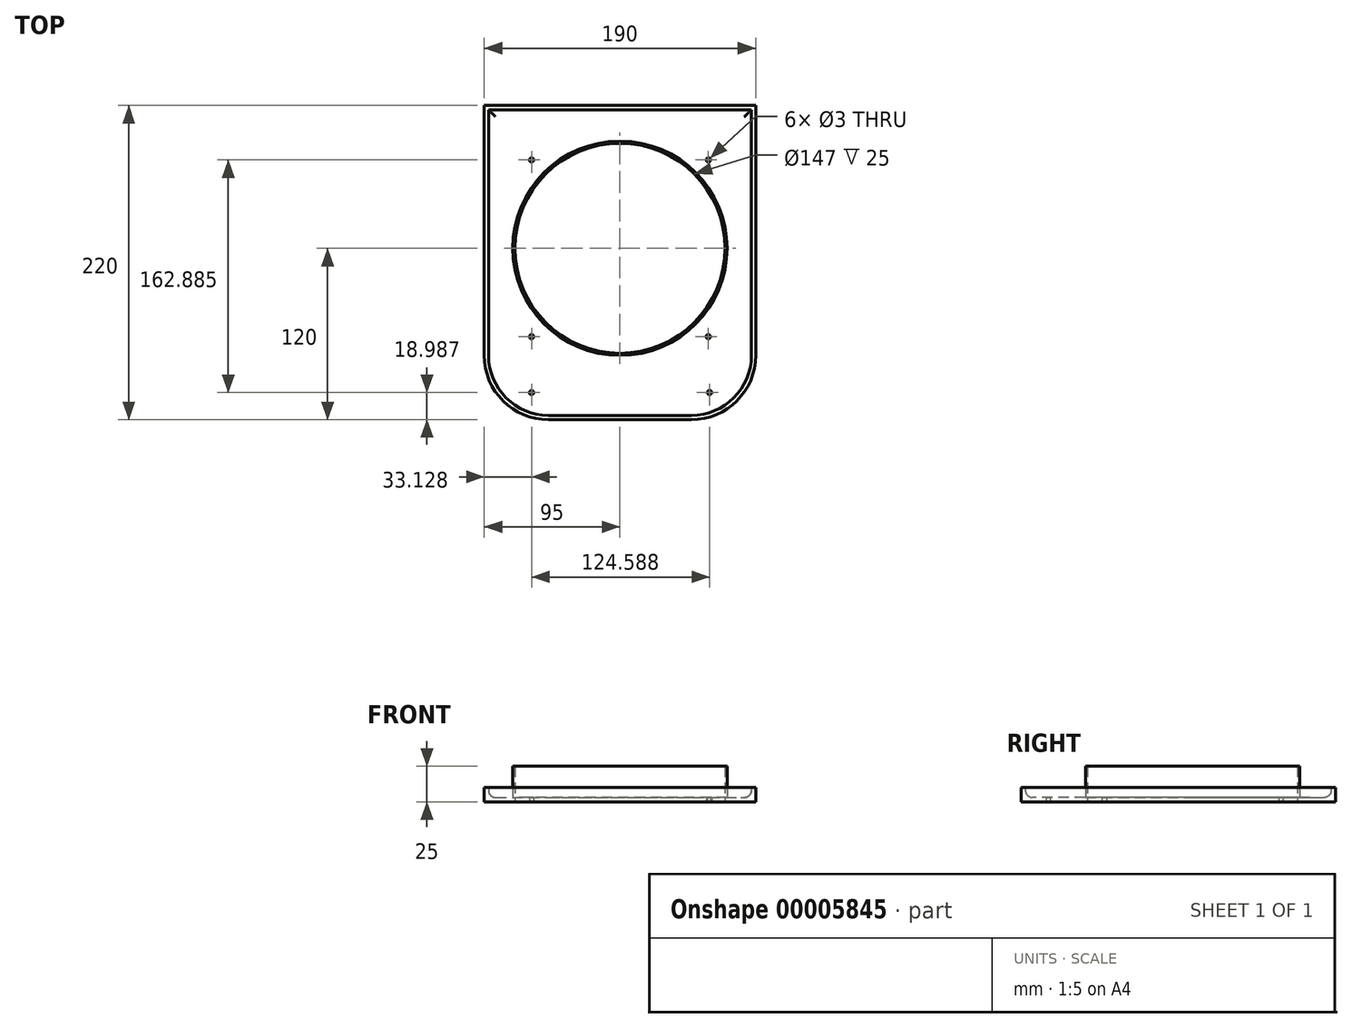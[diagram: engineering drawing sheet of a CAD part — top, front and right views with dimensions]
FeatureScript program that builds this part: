
annotation { "Feature Type Name" : "Feature", "Feature Type Description" : "" }
export const myFeature = defineFeature(function(context is Context, id is Id, definition is map)
    precondition{}
    {
        {
            var Q0;
            Q0=qCreatedBy(makeId("Top.planeOp"),FACE);
            var sketch = newSketch(context, id + "F0", { "sketchPlane" : qUnion([Q0])});
            skCircle(sketch, "E0", {"center": v(0, 0) * mm, "radius": 75 * mm});
            skCircle(sketch, "E1", {"center": v(0, 0) * mm, "radius": 73.5 * mm});
            skLineSegment(sketch, "E2", {"start": v(0, 0) * mm, "end": v(0, 133.7) * mm, "construction": true});
            skLineSegment(sketch, "E3", {"start": v(0, 100) * mm, "end": v(100, 100) * mm, "construction": true});
            skLineSegment(sketch, "E4", {"start": v(100, 100) * mm, "end": v(100, -75) * mm, "construction": true});
            skLineSegment(sketch, "E5", {"start": v(50, -125) * mm, "end": v(0, -125) * mm, "construction": true});
            skPoint(sketch, "E6.visualSharp", {"position": v(100, -125) * mm});
            skArc(sketch, "E6.filletArc", {"start": v(50, -125) * mm, "mid": v(85.36, -110.36) * mm, "end": v(100, -75) * mm, "construction": true});
            skLineSegment(sketch, "E7.0.MirrorCS", {"start": v(0, 100) * mm, "end": v(-100, 100) * mm, "construction": true});
            skLineSegment(sketch, "E7.1.MirrorCS", {"start": v(-50, -125) * mm, "end": v(0, -125) * mm, "construction": true});
            skLineSegment(sketch, "E7.2.MirrorCS", {"start": v(-100, 100) * mm, "end": v(-100, -75) * mm, "construction": true});
            skArc(sketch, "E7.3.MirrorCS", {"start": v(-50, -125) * mm, "mid": v(-85.36, -110.36) * mm, "end": v(-100, -75) * mm, "construction": true});
            skLineSegment(sketch, "E8", {"start": v(95, 100) * mm, "end": v(-95, 100) * mm});
            skLineSegment(sketch, "E9.0", {"start": v(57.6, 97) * mm, "end": v(-92, 97) * mm});
            skLineSegment(sketch, "E10", {"start": v(-95, 97) * mm, "end": v(-95, 82) * mm});
            skLineSegment(sketch, "E11", {"start": v(-57.6, 82) * mm, "end": v(95, 82) * mm, "construction": true});
            skLineSegment(sketch, "E12.left", {"start": v(-95, 82) * mm, "end": v(-95, 97) * mm});
            skLineSegment(sketch, "E13.1.0.0", {"start": v(-57.6, 97) * mm, "end": v(-57.6, 82) * mm});
            skLineSegment(sketch, "E13.1.0.1", {"start": v(-54.6, 82) * mm, "end": v(-54.6, 97) * mm});
            skLineSegment(sketch, "E13.1.0.2", {"start": v(-57.6, 97) * mm, "end": v(-54.6, 97) * mm});
            skLineSegment(sketch, "E13.1.0.3", {"start": v(-57.6, 82) * mm, "end": v(-54.6, 82) * mm});
            skLineSegment(sketch, "E13.2.0.0", {"start": v(-20.2, 97) * mm, "end": v(-20.2, 82) * mm});
            skLineSegment(sketch, "E13.2.0.1", {"start": v(-17.2, 82) * mm, "end": v(-17.2, 97) * mm});
            skLineSegment(sketch, "E13.2.0.3", {"start": v(-20.2, 82) * mm, "end": v(-17.2, 82) * mm});
            skLineSegment(sketch, "E13.3.0.0", {"start": v(17.2, 97) * mm, "end": v(17.2, 82) * mm});
            skLineSegment(sketch, "E13.3.0.1", {"start": v(20.2, 82) * mm, "end": v(20.2, 97) * mm});
            skLineSegment(sketch, "E13.3.0.3", {"start": v(17.2, 82) * mm, "end": v(20.2, 82) * mm});
            skLineSegment(sketch, "E13.4.0.0", {"start": v(54.6, 97) * mm, "end": v(54.6, 82) * mm});
            skLineSegment(sketch, "E13.4.0.1", {"start": v(57.6, 82) * mm, "end": v(57.6, 97) * mm});
            skLineSegment(sketch, "E13.4.0.3", {"start": v(54.6, 82) * mm, "end": v(57.6, 82) * mm});
            skLineSegment(sketch, "E13.direction1", {"start": v(-92, 82) * mm, "end": v(-57.6, 82) * mm, "construction": true});
            skLineSegment(sketch, "E14.0.5.0", {"start": v(92, 97) * mm, "end": v(92, 82) * mm});
            skLineSegment(sketch, "E14.9.5.0", {"start": v(92, 82) * mm, "end": v(95, 82) * mm});
            skLineSegment(sketch, "E15", {"start": v(0, 0) * mm, "end": v(128.67, 128.67) * mm, "construction": true});
            skCircle(sketch, "E16", {"center": v(61.87, 61.87) * mm, "radius": 1.5 * mm});
            skCircle(sketch, "E17.1.0", {"center": v(-61.87, 61.87) * mm, "radius": 1.5 * mm});
            skCircle(sketch, "E17.2.0", {"center": v(-61.87, -61.87) * mm, "radius": 1.5 * mm});
            skCircle(sketch, "E17.3.0", {"center": v(61.87, -61.87) * mm, "radius": 1.5 * mm});
            skCircle(sketch, "E18", {"center": v(0, 0) * mm, "radius": 87.5 * mm, "construction": true});
            skArc(sketch, "E19.1", {"start": v(50, -120) * mm, "mid": v(81.82, -106.82) * mm, "end": v(95, -75) * mm});
            skLineSegment(sketch, "E19.2", {"start": v(50, -120) * mm, "end": v(0, -120) * mm});
            skLineSegment(sketch, "E19.3", {"start": v(-50, -120) * mm, "end": v(0, -120) * mm});
            skArc(sketch, "E19.4", {"start": v(-50, -120) * mm, "mid": v(-81.82, -106.82) * mm, "end": v(-95, -75) * mm});
            skCircle(sketch, "E20", {"center": v(-61.87, -101.01) * mm, "radius": 1.5 * mm});
            skCircle(sketch, "E21", {"center": v(62.72, -101.01) * mm, "radius": 1.5 * mm});
            skLineSegment(sketch, "E22", {"start": v(-95, 100) * mm, "end": v(-95, -75) * mm});
            skArc(sketch, "E23.1", {"start": v(50, -117) * mm, "mid": v(79.7, -104.7) * mm, "end": v(92, -75) * mm});
            skLineSegment(sketch, "E23.2", {"start": v(50, -117) * mm, "end": v(0, -117) * mm});
            skLineSegment(sketch, "E23.3", {"start": v(-50, -117) * mm, "end": v(0, -117) * mm});
            skArc(sketch, "E23.4", {"start": v(-50, -117) * mm, "mid": v(-79.7, -104.7) * mm, "end": v(-92, -75) * mm});
            skLineSegment(sketch, "E23.5", {"start": v(-92, 97) * mm, "end": v(-92, -75) * mm});
            skLineSegment(sketch, "E24", {"start": v(95, 82) * mm, "end": v(95, 100) * mm});
            skLineSegment(sketch, "E25", {"start": v(57.6, 97) * mm, "end": v(92, 97) * mm});
            skLineSegment(sketch, "E26", {"start": v(92, -75) * mm, "end": v(92, 82) * mm});
            skLineSegment(sketch, "E27", {"start": v(95, -75) * mm, "end": v(95, 82) * mm});
            skLineSegment(sketch, "E28", {"start": v(-95, 82) * mm, "end": v(-92, 82) * mm});
            skSolve(sketch);
        }
        {
            var Q0;
            Q0=makeQuery(id+"F0.imprint","IMPRINT",FACE,{"disambiguationData":[TD([[makeQuery(id+"F0.imprint","IMPRINT",EDGE,{"derivedFrom":sQuery(id+"F0.wireOp",EDGE,"E0")}),-1.0]])]});
            var Q1;
            {var subQ1=sQuery(id+"F0.wireOp",EDGE,"E13.4.0.0");Q1=makeQuery(id+"F0.imprint","IMPRINT",FACE,{"disambiguationData":[TD([[makeQuery(id+"F0.imprint","IMPRINT",EDGE,{"derivedFrom":subQ1}),1.0]])]});}
            var Q2;
            {var subQ1=sQuery(id+"F0.wireOp",EDGE,"E13.3.0.0");Q2=makeQuery(id+"F0.imprint","IMPRINT",FACE,{"disambiguationData":[TD([[makeQuery(id+"F0.imprint","IMPRINT",EDGE,{"derivedFrom":subQ1}),1.0]])]});}
            var Q3;
            {var subQ1=sQuery(id+"F0.wireOp",EDGE,"E13.2.0.0");Q3=makeQuery(id+"F0.imprint","IMPRINT",FACE,{"disambiguationData":[TD([[makeQuery(id+"F0.imprint","IMPRINT",EDGE,{"derivedFrom":subQ1}),1.0]])]});}
            var Q4;
            Q4=makeQuery(id+"F0.imprint","IMPRINT",FACE,{"disambiguationData":[TD([[makeQuery(id+"F0.imprint","IMPRINT",EDGE,{"derivedFrom":sQuery(id+"F0.wireOp",EDGE,"E13.1.0.0")}),1.0]])]});
            var Q5;
            Q5=makeQuery(id+"F0.imprint","IMPRINT",FACE,{"disambiguationData":[TD([[makeQuery(id+"F0.imprint","IMPRINT",EDGE,{"derivedFrom":sQuery(id+"F0.wireOp",EDGE,"E19.1")}),1.0]])]});
            var Q6;
            {var subQ3=sQuery(id+"F0.wireOp",EDGE,"E8");Q6=makeQuery(id+"F0.imprint","IMPRINT",FACE,{"disambiguationData":[TD([[makeQuery(id+"F0.imprint","IMPRINT",EDGE,{"derivedFrom":subQ3}),1.0]])]});}
            extrude(context, id + "F1", {"entities" : qUnion([Q0, Q1, Q2, Q3, Q4, Q5, Q6]), "depth" : 3 * mm});
        }
        {
            var Q0;
            Q0=makeQuery(id+"F0.imprint","IMPRINT",FACE,{"disambiguationData":[TD([[makeQuery(id+"F0.imprint","IMPRINT",EDGE,{"derivedFrom":sQuery(id+"F0.wireOp",EDGE,"E0")}),1.0]])]});
            extrude(context, id + "F2", {"entities" : qUnion([Q0]), "operationType" : NewBodyOperationType.ADD, "depth" : 25 * mm});
        }
        {
            var Q0;
            Q0=makeQuery(id+"F0.imprint","IMPRINT",FACE,{"disambiguationData":[TD([[makeQuery(id+"F0.imprint","IMPRINT",EDGE,{"derivedFrom":sQuery(id+"F0.wireOp",EDGE,"E19.1")}),1.0]])]});
            var Q1;
            {var subQ3=sQuery(id+"F0.wireOp",EDGE,"E8");Q1=makeQuery(id+"F0.imprint","IMPRINT",FACE,{"disambiguationData":[TD([[makeQuery(id+"F0.imprint","IMPRINT",EDGE,{"derivedFrom":subQ3}),1.0]])]});}
            extrude(context, id + "F3", {"entities" : qUnion([Q0, Q1]), "operationType" : NewBodyOperationType.ADD, "depth" : 10 * mm});
        }
        {
            var Q0;
            Q0=makeQuery(id+"F3.boolean.opBoolean","INTERSECT",EDGE,{"derivedFrom":[makeQuery(id+"F1.opExtrude","CAP_FACE",FACE,{"disambiguationData":[OSD([sQuery(id+"F0.wireOp",EDGE,"E0"),sQuery(id+"F0.wireOp",EDGE,"E8"),sQuery(id+"F0.wireOp",EDGE,"E16"),sQuery(id+"F0.wireOp",EDGE,"E17.1.0"),sQuery(id+"F0.wireOp",EDGE,"E17.2.0"),sQuery(id+"F0.wireOp",EDGE,"E17.3.0"),sQuery(id+"F0.wireOp",EDGE,"E19.1"),sQuery(id+"F0.wireOp",EDGE,"E19.2"),sQuery(id+"F0.wireOp",EDGE,"E19.3"),sQuery(id+"F0.wireOp",EDGE,"E19.4"),sQuery(id+"F0.wireOp",EDGE,"E20"),sQuery(id+"F0.wireOp",EDGE,"E21"),sQuery(id+"F0.wireOp",EDGE,"E22"),sQuery(id+"F0.wireOp",EDGE,"E24"),sQuery(id+"F0.wireOp",EDGE,"E27")])],"isStart":false}),makeQuery(id+"F3.opExtrude","SWEPT_FACE",FACE,{"disambiguationData":[OSD([sQuery(id+"F0.wireOp",EDGE,"E23.1")])]})]});
            var Q1;
            Q1=makeQuery(id+"F3.boolean.opBoolean","INTERSECT",EDGE,{"derivedFrom":[makeQuery(id+"F1.opExtrude","CAP_FACE",FACE,{"disambiguationData":[OSD([sQuery(id+"F0.wireOp",EDGE,"E0"),sQuery(id+"F0.wireOp",EDGE,"E8"),sQuery(id+"F0.wireOp",EDGE,"E16"),sQuery(id+"F0.wireOp",EDGE,"E17.1.0"),sQuery(id+"F0.wireOp",EDGE,"E17.2.0"),sQuery(id+"F0.wireOp",EDGE,"E17.3.0"),sQuery(id+"F0.wireOp",EDGE,"E19.1"),sQuery(id+"F0.wireOp",EDGE,"E19.2"),sQuery(id+"F0.wireOp",EDGE,"E19.3"),sQuery(id+"F0.wireOp",EDGE,"E19.4"),sQuery(id+"F0.wireOp",EDGE,"E20"),sQuery(id+"F0.wireOp",EDGE,"E21"),sQuery(id+"F0.wireOp",EDGE,"E22"),sQuery(id+"F0.wireOp",EDGE,"E24"),sQuery(id+"F0.wireOp",EDGE,"E27")])],"isStart":false}),makeQuery(id+"F3.opExtrude","SWEPT_FACE",FACE,{"disambiguationData":[OSD([sQuery(id+"F0.wireOp",EDGE,"E9.0"),sQuery(id+"F0.wireOp",EDGE,"E13.1.0.2"),sQuery(id+"F0.wireOp",EDGE,"E25")])]})]});
            var Q2;
            Q2=makeQuery(id+"F1.opExtrude","CAP_EDGE",EDGE,{"disambiguationData":[OSD([sQuery(id+"F0.wireOp",EDGE,"E0")])],"isStart":false});
            fillet(context, id + "F4", {"entities" : qUnion([Q0, Q1, Q2]), "radius" : 5 * mm, "tangentPropagation" : true, "allowEdgeOverflow" : false});
        }
    });
